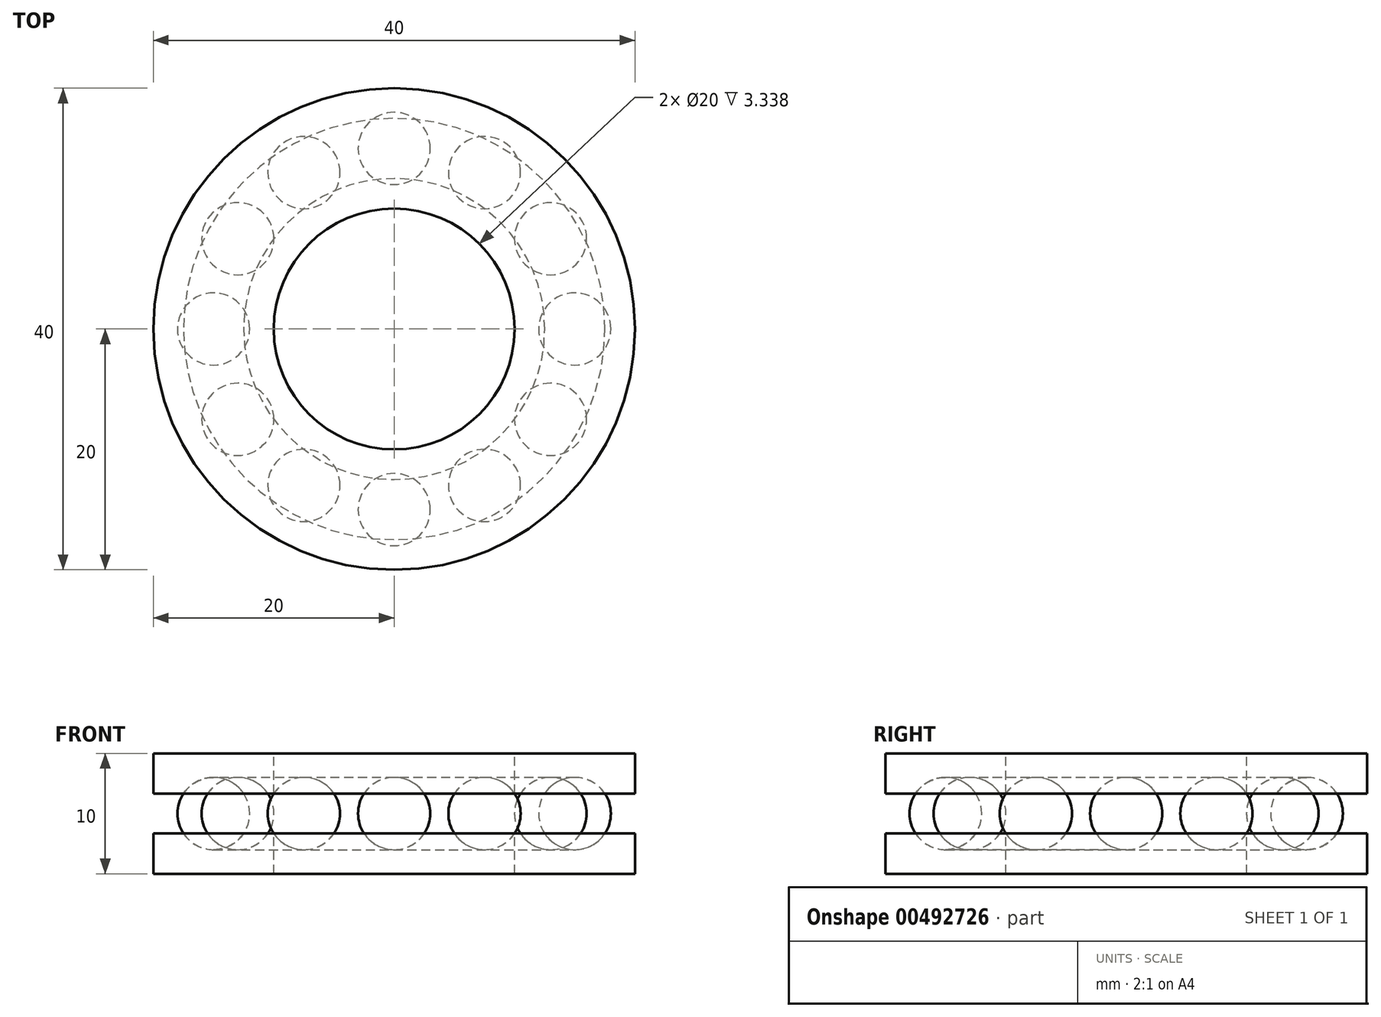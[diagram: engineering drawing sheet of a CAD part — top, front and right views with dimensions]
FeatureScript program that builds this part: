
annotation { "Feature Type Name" : "Feature", "Feature Type Description" : "" }
export const myFeature = defineFeature(function(context is Context, id is Id, definition is map)
    precondition{}
    {
        {
            var Q0;
            Q0=qCreatedBy(makeId("Front.planeOp"),FACE);
            var sketch = newSketch(context, id + "F0", { "sketchPlane" : qUnion([Q0])});
            skLineSegment(sketch, "E0", {"start": v(0, 22.1) * mm, "end": v(0, -38.3) * mm, "construction": true});
            skLineSegment(sketch, "E1.bottom", {"start": v(-10, 0) * mm, "end": v(-20, 0) * mm});
            skLineSegment(sketch, "E1.top", {"start": v(-10, 10) * mm, "end": v(-20, 10) * mm});
            skLineSegment(sketch, "E1.left", {"start": v(-10, 0) * mm, "end": v(-10, 3.34) * mm});
            skLineSegment(sketch, "E1.right", {"start": v(-20, 0) * mm, "end": v(-20, 3.34) * mm});
            skArc(sketch, "E2", {"start": v(-17.5, 3.34) * mm, "mid": v(-15, 2) * mm, "end": v(-12.5, 3.34) * mm});
            skPoint(sketch, "E2.centerSnap0", {"position": v(-10, 5) * mm});
            skPoint(sketch, "E2.centerSnap1", {"position": v(-15, 0) * mm});
            skLineSegment(sketch, "E3", {"start": v(-23.2, 5) * mm, "end": v(-5.95, 5) * mm, "construction": true});
            skPoint(sketch, "E3.endSnap0", {"position": v(-20, 5) * mm});
            skLineSegment(sketch, "E4", {"start": v(-20, 6.66) * mm, "end": v(-17.5, 6.66) * mm});
            skLineSegment(sketch, "E5.MirrorCS", {"start": v(-20, 3.34) * mm, "end": v(-17.5, 3.34) * mm});
            skLineSegment(sketch, "E6.trimOffspring", {"start": v(-20, 6.66) * mm, "end": v(-20, 10) * mm});
            skLineSegment(sketch, "E7.trimOffspring", {"start": v(-12.5, 3.34) * mm, "end": v(-10, 3.34) * mm});
            skArc(sketch, "E8.trimOffspring", {"start": v(-12.5, 6.66) * mm, "mid": v(-15, 8) * mm, "end": v(-17.5, 6.66) * mm});
            skLineSegment(sketch, "E9.trimOffspring", {"start": v(-12.5, 6.66) * mm, "end": v(-10, 6.66) * mm});
            skLineSegment(sketch, "E10.trimOffspring", {"start": v(-10, 6.66) * mm, "end": v(-10, 10) * mm});
            skLineSegment(sketch, "E11", {"start": v(-15, 12.46) * mm, "end": v(-15, -2.7) * mm, "construction": true});
            skPoint(sketch, "E11.startSnap0", {"position": v(-15, 10) * mm});
            skArc(sketch, "E12", {"start": v(-12.5, 6.66) * mm, "mid": v(-18, 5) * mm, "end": v(-12.5, 3.34) * mm});
            skLineSegment(sketch, "E13", {"start": v(-15, 8) * mm, "end": v(-15, 2) * mm});
            skSolve(sketch);
        }
        {
            var Q0;
            {var subQ2=sQuery(id+"F0.wireOp",EDGE,"E12");Q0=makeQuery(id+"F0.imprint","IMPRINT",FACE,{"disambiguationData":[TD([[makeQuery(id+"F0.imprint","IMPRINT",EDGE,{"derivedFrom":subQ2}),1.0]])]});}
            var Q1;
            Q1=sQuery(id+"F0.wireOp",EDGE,"E13");
            revolve(context, id + "F1", {"entities" : qUnion([Q0]), "axis" : qUnion([Q1]), "revolveType" : RevolveType.FULL});
        }
        {
            var Q0;
            Q0=makeQuery(id+"F0.imprint","IMPRINT",FACE,{"disambiguationData":[TD([[makeQuery(id+"F0.imprint","IMPRINT",EDGE,{"derivedFrom":sQuery(id+"F0.wireOp",EDGE,"E1.top")}),1.0]])]});
            var Q1;
            Q1=makeQuery(id+"F0.imprint","IMPRINT",FACE,{"disambiguationData":[TD([[makeQuery(id+"F0.imprint","IMPRINT",EDGE,{"derivedFrom":sQuery(id+"F0.wireOp",EDGE,"E1.bottom")}),-1.0]])]});
            var Q2;
            Q2=sQuery(id+"F0.wireOp",EDGE,"E0");
            revolve(context, id + "F2", {"operationType" : NewBodyOperationType.ADD, "entities" : qUnion([Q0, Q1]), "axis" : qUnion([Q2]), "revolveType" : RevolveType.FULL});
        }
        {
            var Q0;
            Q0=makeQuery(id+"F1.opRevolve","SWEPT_BODY",BODY,{"disambiguationData":[OSD([sQuery(id+"F0.wireOp",EDGE,"E2"),sQuery(id+"F0.wireOp",EDGE,"E8.trimOffspring"),sQuery(id+"F0.wireOp",EDGE,"E12"),sQuery(id+"F0.wireOp",EDGE,"E13")])]});
            var Q1;
            Q1=sQuery(id+"F0.wireOp",EDGE,"E0");
            circularPattern(context, id + "F3", {"entities" : qUnion([Q0]), "axis" : qUnion([Q1]), "angle" : 360 * degree, "instanceCount" : 12, "equalSpace" : true, "computeTransformsWithoutBuiltin" : true});
        }
    });
